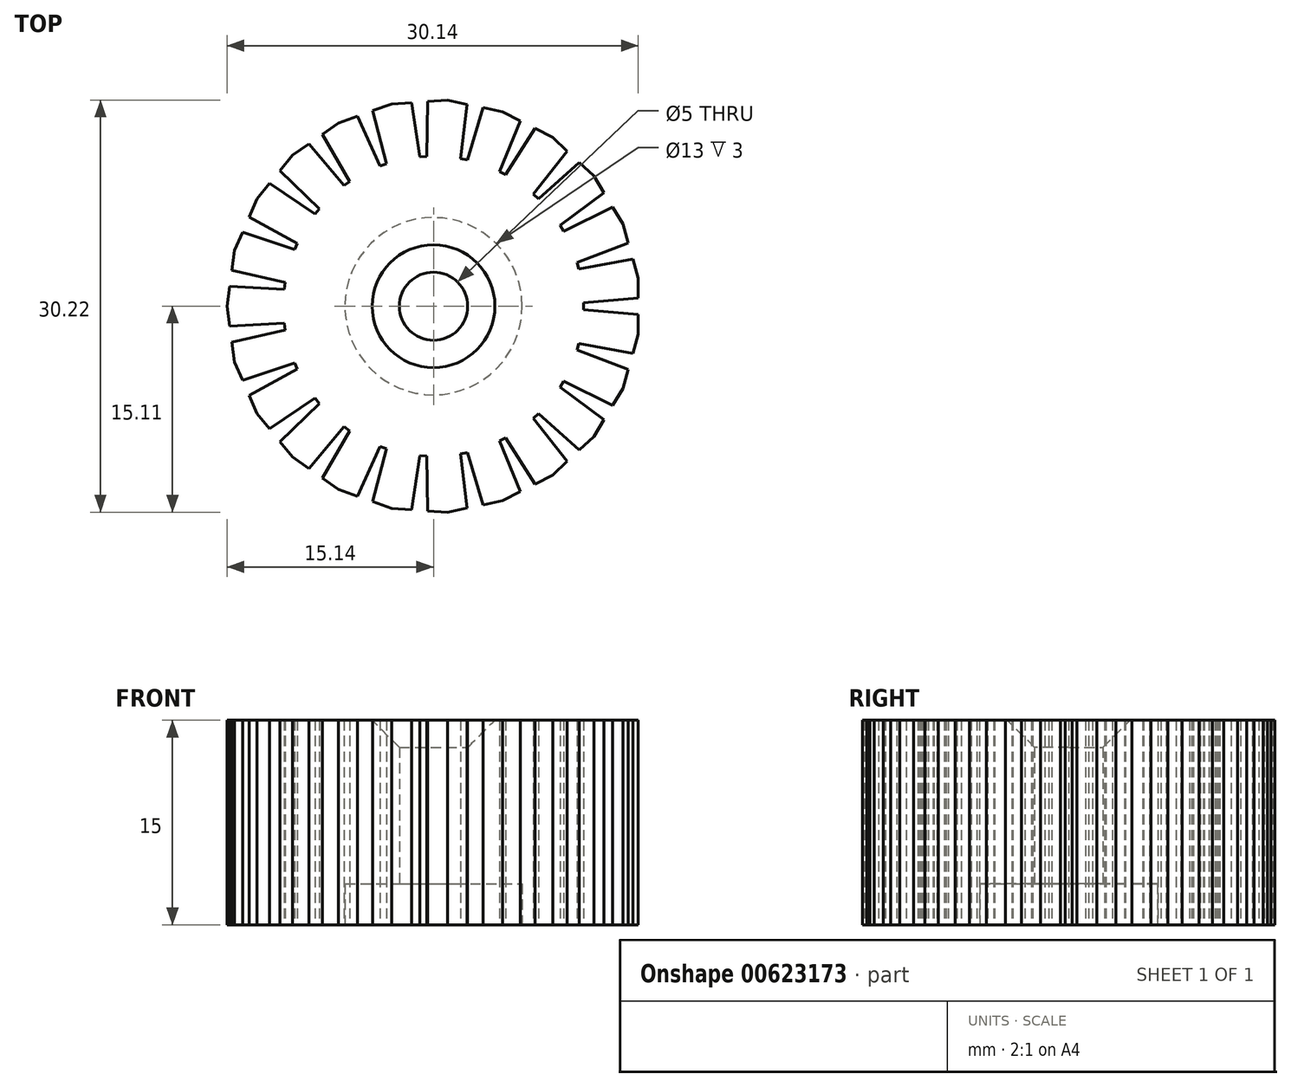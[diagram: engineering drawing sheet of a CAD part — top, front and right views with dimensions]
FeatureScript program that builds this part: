
annotation { "Feature Type Name" : "Feature", "Feature Type Description" : "" }
export const myFeature = defineFeature(function(context is Context, id is Id, definition is map)
    precondition{}
    {
        {
            var Q0;
            Q0=qCreatedBy(makeId("Top.planeOp"),FACE);
            var sketch = newSketch(context, id + "F0", { "sketchPlane" : qUnion([Q0])});
            skCircle(sketch, "E0", {"center": v(0, 0) * mm, "radius": 2.5 * mm});
            skCircle(sketch, "E1.cCircle", {"center": v(0, 0) * mm, "radius": 15 * mm, "construction": true});
            skLineSegment(sketch, "E1.0", {"start": v(15, 2.06) * mm, "end": v(15, 0.6) * mm});
            skLineSegment(sketch, "E1.1", {"start": v(15, -2.06) * mm, "end": v(13.89, -6.03) * mm, "construction": true});
            skLineSegment(sketch, "E1.2", {"start": v(13.89, -6.03) * mm, "end": v(11.75, -9.56) * mm, "construction": true});
            skLineSegment(sketch, "E1.3", {"start": v(11.75, -9.56) * mm, "end": v(8.73, -12.37) * mm, "construction": true});
            skLineSegment(sketch, "E1.4", {"start": v(8.73, -12.37) * mm, "end": v(5.07, -14.27) * mm, "construction": true});
            skLineSegment(sketch, "E1.5", {"start": v(5.07, -14.27) * mm, "end": v(1.03, -15.1) * mm, "construction": true});
            skLineSegment(sketch, "E1.6", {"start": v(1.03, -15.1) * mm, "end": v(-3.08, -14.82) * mm, "construction": true});
            skLineSegment(sketch, "E1.7", {"start": v(-3.08, -14.82) * mm, "end": v(-6.97, -13.44) * mm, "construction": true});
            skLineSegment(sketch, "E1.8", {"start": v(-6.97, -13.44) * mm, "end": v(-10.33, -11.07) * mm, "construction": true});
            skLineSegment(sketch, "E1.9", {"start": v(-10.33, -11.07) * mm, "end": v(-12.94, -7.87) * mm, "construction": true});
            skLineSegment(sketch, "E1.10", {"start": v(-12.94, -7.87) * mm, "end": v(-14.58, -4.08) * mm, "construction": true});
            skLineSegment(sketch, "E1.11", {"start": v(-14.58, -4.08) * mm, "end": v(-15.14, 0) * mm, "construction": true});
            skLineSegment(sketch, "E1.12", {"start": v(-15.14, 0) * mm, "end": v(-14.58, 4.08) * mm, "construction": true});
            skLineSegment(sketch, "E1.13", {"start": v(-14.58, 4.08) * mm, "end": v(-12.94, 7.87) * mm, "construction": true});
            skLineSegment(sketch, "E1.14", {"start": v(-12.94, 7.87) * mm, "end": v(-10.33, 11.07) * mm, "construction": true});
            skLineSegment(sketch, "E1.15", {"start": v(-10.33, 11.07) * mm, "end": v(-6.97, 13.44) * mm, "construction": true});
            skLineSegment(sketch, "E1.16", {"start": v(-6.97, 13.44) * mm, "end": v(-3.08, 14.82) * mm, "construction": true});
            skLineSegment(sketch, "E1.17", {"start": v(-3.08, 14.82) * mm, "end": v(1.03, 15.1) * mm, "construction": true});
            skLineSegment(sketch, "E1.18", {"start": v(1.03, 15.1) * mm, "end": v(5.07, 14.27) * mm, "construction": true});
            skLineSegment(sketch, "E1.19", {"start": v(5.07, 14.27) * mm, "end": v(8.73, 12.37) * mm, "construction": true});
            skLineSegment(sketch, "E1.20", {"start": v(8.73, 12.37) * mm, "end": v(11.75, 9.56) * mm, "construction": true});
            skLineSegment(sketch, "E1.21", {"start": v(11.75, 9.56) * mm, "end": v(13.89, 6.03) * mm, "construction": true});
            skLineSegment(sketch, "E1.22", {"start": v(13.89, 6.03) * mm, "end": v(15, 2.06) * mm, "construction": true});
            skPoint(sketch, "E1.0.midPoint", {"position": v(15, 0) * mm});
            skLineSegment(sketch, "E2", {"start": v(15, 0.6) * mm, "end": v(11, 0.25) * mm});
            skLineSegment(sketch, "E3", {"start": v(11, 0.25) * mm, "end": v(11, -0.25) * mm});
            skLineSegment(sketch, "E4", {"start": v(11, -0.25) * mm, "end": v(15, -0.6) * mm});
            skLineSegment(sketch, "E5.trimOffspring", {"start": v(15, -0.6) * mm, "end": v(15, -2.06) * mm});
            skLineSegment(sketch, "E6.1.0", {"start": v(13.89, 6.03) * mm, "end": v(14.28, 4.62) * mm});
            skLineSegment(sketch, "E6.1.1", {"start": v(14.28, 4.62) * mm, "end": v(10.52, 3.2) * mm});
            skLineSegment(sketch, "E6.1.2", {"start": v(10.66, 2.73) * mm, "end": v(14.6, 3.47) * mm});
            skLineSegment(sketch, "E6.1.3", {"start": v(10.52, 3.2) * mm, "end": v(10.66, 2.73) * mm});
            skLineSegment(sketch, "E6.1.4", {"start": v(14.6, 3.47) * mm, "end": v(15, 2.06) * mm});
            skLineSegment(sketch, "E6.2.0", {"start": v(11.75, 9.56) * mm, "end": v(12.5, 8.3) * mm});
            skLineSegment(sketch, "E6.2.1", {"start": v(12.5, 8.3) * mm, "end": v(9.27, 5.93) * mm});
            skLineSegment(sketch, "E6.2.2", {"start": v(9.53, 5.5) * mm, "end": v(13.13, 7.28) * mm});
            skLineSegment(sketch, "E6.2.3", {"start": v(9.27, 5.93) * mm, "end": v(9.53, 5.5) * mm});
            skLineSegment(sketch, "E6.2.4", {"start": v(13.13, 7.28) * mm, "end": v(13.89, 6.03) * mm});
            skLineSegment(sketch, "E6.3.0", {"start": v(8.73, 12.37) * mm, "end": v(9.8, 11.37) * mm});
            skLineSegment(sketch, "E6.3.1", {"start": v(9.8, 11.37) * mm, "end": v(7.33, 8.2) * mm});
            skLineSegment(sketch, "E6.3.2", {"start": v(7.7, 7.87) * mm, "end": v(10.68, 10.55) * mm});
            skLineSegment(sketch, "E6.3.3", {"start": v(7.33, 8.2) * mm, "end": v(7.7, 7.87) * mm});
            skLineSegment(sketch, "E6.3.4", {"start": v(10.68, 10.55) * mm, "end": v(11.75, 9.56) * mm});
            skLineSegment(sketch, "E6.4.0", {"start": v(5.07, 14.27) * mm, "end": v(6.37, 13.6) * mm});
            skLineSegment(sketch, "E6.4.1", {"start": v(6.37, 13.6) * mm, "end": v(4.84, 9.88) * mm});
            skLineSegment(sketch, "E6.4.2", {"start": v(5.28, 9.65) * mm, "end": v(7.43, 13.04) * mm});
            skLineSegment(sketch, "E6.4.3", {"start": v(4.84, 9.88) * mm, "end": v(5.28, 9.65) * mm});
            skLineSegment(sketch, "E6.4.4", {"start": v(7.43, 13.04) * mm, "end": v(8.73, 12.37) * mm});
            skLineSegment(sketch, "E6.5.0", {"start": v(1.03, 15.1) * mm, "end": v(2.46, 14.8) * mm});
            skLineSegment(sketch, "E6.5.1", {"start": v(2.46, 14.8) * mm, "end": v(2, 10.82) * mm});
            skLineSegment(sketch, "E6.5.2", {"start": v(2.48, 10.72) * mm, "end": v(3.64, 14.56) * mm});
            skLineSegment(sketch, "E6.5.3", {"start": v(2, 10.82) * mm, "end": v(2.48, 10.72) * mm});
            skLineSegment(sketch, "E6.5.4", {"start": v(3.64, 14.56) * mm, "end": v(5.07, 14.27) * mm});
            skLineSegment(sketch, "E6.6.0", {"start": v(-3.08, 14.82) * mm, "end": v(-1.62, 14.92) * mm});
            skLineSegment(sketch, "E6.6.1", {"start": v(-1.62, 14.92) * mm, "end": v(-1, 10.96) * mm});
            skLineSegment(sketch, "E6.6.2", {"start": v(-0.5, 11) * mm, "end": v(-0.43, 15) * mm});
            skLineSegment(sketch, "E6.6.3", {"start": v(-1, 10.96) * mm, "end": v(-0.5, 11) * mm});
            skLineSegment(sketch, "E6.6.4", {"start": v(-0.43, 15) * mm, "end": v(1.03, 15.1) * mm});
            skLineSegment(sketch, "E6.7.0", {"start": v(-6.97, 13.44) * mm, "end": v(-5.59, 13.93) * mm});
            skLineSegment(sketch, "E6.7.1", {"start": v(-5.59, 13.93) * mm, "end": v(-3.92, 10.28) * mm});
            skLineSegment(sketch, "E6.7.2", {"start": v(-3.45, 10.45) * mm, "end": v(-4.46, 14.33) * mm});
            skLineSegment(sketch, "E6.7.3", {"start": v(-3.92, 10.28) * mm, "end": v(-3.45, 10.45) * mm});
            skLineSegment(sketch, "E6.7.4", {"start": v(-4.46, 14.33) * mm, "end": v(-3.08, 14.82) * mm});
            skLineSegment(sketch, "E6.8.0", {"start": v(-10.33, 11.07) * mm, "end": v(-9.14, 11.9) * mm});
            skLineSegment(sketch, "E6.8.1", {"start": v(-9.14, 11.9) * mm, "end": v(-6.55, 8.84) * mm});
            skLineSegment(sketch, "E6.8.2", {"start": v(-6.14, 9.13) * mm, "end": v(-8.16, 12.6) * mm});
            skLineSegment(sketch, "E6.8.3", {"start": v(-6.55, 8.84) * mm, "end": v(-6.14, 9.13) * mm});
            skLineSegment(sketch, "E6.8.4", {"start": v(-8.16, 12.6) * mm, "end": v(-6.97, 13.44) * mm});
            skLineSegment(sketch, "E6.9.0", {"start": v(-12.94, 7.87) * mm, "end": v(-12.01, 9) * mm});
            skLineSegment(sketch, "E6.9.1", {"start": v(-12.01, 9) * mm, "end": v(-8.7, 6.75) * mm});
            skLineSegment(sketch, "E6.9.2", {"start": v(-8.38, 7.14) * mm, "end": v(-11.26, 9.93) * mm});
            skLineSegment(sketch, "E6.9.3", {"start": v(-8.7, 6.75) * mm, "end": v(-8.38, 7.14) * mm});
            skLineSegment(sketch, "E6.9.4", {"start": v(-11.26, 9.93) * mm, "end": v(-10.33, 11.07) * mm});
            skLineSegment(sketch, "E6.10.0", {"start": v(-14.58, 4.08) * mm, "end": v(-14, 5.43) * mm});
            skLineSegment(sketch, "E6.10.1", {"start": v(-14, 5.43) * mm, "end": v(-10.19, 4.15) * mm});
            skLineSegment(sketch, "E6.10.2", {"start": v(-9.99, 4.61) * mm, "end": v(-13.52, 6.53) * mm});
            skLineSegment(sketch, "E6.10.3", {"start": v(-10.19, 4.15) * mm, "end": v(-9.99, 4.61) * mm});
            skLineSegment(sketch, "E6.10.4", {"start": v(-13.52, 6.53) * mm, "end": v(-12.94, 7.87) * mm});
            skLineSegment(sketch, "E6.11.0", {"start": v(-15.14, 0) * mm, "end": v(-14.94, 1.45) * mm});
            skLineSegment(sketch, "E6.11.1", {"start": v(-14.94, 1.45) * mm, "end": v(-10.93, 1.25) * mm});
            skLineSegment(sketch, "E6.11.2", {"start": v(-10.86, 1.75) * mm, "end": v(-14.78, 2.64) * mm});
            skLineSegment(sketch, "E6.11.3", {"start": v(-10.93, 1.25) * mm, "end": v(-10.86, 1.75) * mm});
            skLineSegment(sketch, "E6.11.4", {"start": v(-14.78, 2.64) * mm, "end": v(-14.58, 4.08) * mm});
            skLineSegment(sketch, "E6.12.0", {"start": v(-14.58, -4.08) * mm, "end": v(-14.78, -2.64) * mm});
            skLineSegment(sketch, "E6.12.1", {"start": v(-14.78, -2.64) * mm, "end": v(-10.86, -1.75) * mm});
            skLineSegment(sketch, "E6.12.2", {"start": v(-10.93, -1.25) * mm, "end": v(-14.94, -1.45) * mm});
            skLineSegment(sketch, "E6.12.3", {"start": v(-10.86, -1.75) * mm, "end": v(-10.93, -1.25) * mm});
            skLineSegment(sketch, "E6.12.4", {"start": v(-14.94, -1.45) * mm, "end": v(-15.14, 0) * mm});
            skLineSegment(sketch, "E6.13.0", {"start": v(-12.94, -7.87) * mm, "end": v(-13.52, -6.53) * mm});
            skLineSegment(sketch, "E6.13.1", {"start": v(-13.52, -6.53) * mm, "end": v(-9.99, -4.61) * mm});
            skLineSegment(sketch, "E6.13.2", {"start": v(-10.19, -4.15) * mm, "end": v(-14, -5.43) * mm});
            skLineSegment(sketch, "E6.13.3", {"start": v(-9.99, -4.61) * mm, "end": v(-10.19, -4.15) * mm});
            skLineSegment(sketch, "E6.13.4", {"start": v(-14, -5.43) * mm, "end": v(-14.58, -4.08) * mm});
            skLineSegment(sketch, "E6.14.0", {"start": v(-10.33, -11.07) * mm, "end": v(-11.26, -9.93) * mm});
            skLineSegment(sketch, "E6.14.1", {"start": v(-11.26, -9.93) * mm, "end": v(-8.38, -7.14) * mm});
            skLineSegment(sketch, "E6.14.2", {"start": v(-8.7, -6.75) * mm, "end": v(-12.01, -9) * mm});
            skLineSegment(sketch, "E6.14.3", {"start": v(-8.38, -7.14) * mm, "end": v(-8.7, -6.75) * mm});
            skLineSegment(sketch, "E6.14.4", {"start": v(-12.01, -9) * mm, "end": v(-12.94, -7.87) * mm});
            skLineSegment(sketch, "E6.15.0", {"start": v(-6.97, -13.44) * mm, "end": v(-8.16, -12.6) * mm});
            skLineSegment(sketch, "E6.15.1", {"start": v(-8.16, -12.6) * mm, "end": v(-6.14, -9.13) * mm});
            skLineSegment(sketch, "E6.15.2", {"start": v(-6.55, -8.84) * mm, "end": v(-9.14, -11.9) * mm});
            skLineSegment(sketch, "E6.15.3", {"start": v(-6.14, -9.13) * mm, "end": v(-6.55, -8.84) * mm});
            skLineSegment(sketch, "E6.15.4", {"start": v(-9.14, -11.9) * mm, "end": v(-10.33, -11.07) * mm});
            skLineSegment(sketch, "E6.16.0", {"start": v(-3.08, -14.82) * mm, "end": v(-4.46, -14.33) * mm});
            skLineSegment(sketch, "E6.16.1", {"start": v(-4.46, -14.33) * mm, "end": v(-3.45, -10.45) * mm});
            skLineSegment(sketch, "E6.16.2", {"start": v(-3.92, -10.28) * mm, "end": v(-5.59, -13.93) * mm});
            skLineSegment(sketch, "E6.16.3", {"start": v(-3.45, -10.45) * mm, "end": v(-3.92, -10.28) * mm});
            skLineSegment(sketch, "E6.16.4", {"start": v(-5.59, -13.93) * mm, "end": v(-6.97, -13.44) * mm});
            skLineSegment(sketch, "E6.17.0", {"start": v(1.03, -15.1) * mm, "end": v(-0.43, -15) * mm});
            skLineSegment(sketch, "E6.17.1", {"start": v(-0.43, -15) * mm, "end": v(-0.5, -11) * mm});
            skLineSegment(sketch, "E6.17.2", {"start": v(-1, -10.96) * mm, "end": v(-1.62, -14.92) * mm});
            skLineSegment(sketch, "E6.17.3", {"start": v(-0.5, -11) * mm, "end": v(-1, -10.96) * mm});
            skLineSegment(sketch, "E6.17.4", {"start": v(-1.62, -14.92) * mm, "end": v(-3.08, -14.82) * mm});
            skLineSegment(sketch, "E6.18.0", {"start": v(5.07, -14.27) * mm, "end": v(3.64, -14.56) * mm});
            skLineSegment(sketch, "E6.18.1", {"start": v(3.64, -14.56) * mm, "end": v(2.48, -10.72) * mm});
            skLineSegment(sketch, "E6.18.2", {"start": v(2, -10.82) * mm, "end": v(2.46, -14.8) * mm});
            skLineSegment(sketch, "E6.18.3", {"start": v(2.48, -10.72) * mm, "end": v(2, -10.82) * mm});
            skLineSegment(sketch, "E6.18.4", {"start": v(2.46, -14.8) * mm, "end": v(1.03, -15.1) * mm});
            skLineSegment(sketch, "E6.19.0", {"start": v(8.73, -12.37) * mm, "end": v(7.43, -13.04) * mm});
            skLineSegment(sketch, "E6.19.1", {"start": v(7.43, -13.04) * mm, "end": v(5.28, -9.65) * mm});
            skLineSegment(sketch, "E6.19.2", {"start": v(4.84, -9.88) * mm, "end": v(6.37, -13.6) * mm});
            skLineSegment(sketch, "E6.19.3", {"start": v(5.28, -9.65) * mm, "end": v(4.84, -9.88) * mm});
            skLineSegment(sketch, "E6.19.4", {"start": v(6.37, -13.6) * mm, "end": v(5.07, -14.27) * mm});
            skLineSegment(sketch, "E6.20.0", {"start": v(11.75, -9.56) * mm, "end": v(10.68, -10.55) * mm});
            skLineSegment(sketch, "E6.20.1", {"start": v(10.68, -10.55) * mm, "end": v(7.7, -7.87) * mm});
            skLineSegment(sketch, "E6.20.2", {"start": v(7.33, -8.2) * mm, "end": v(9.8, -11.37) * mm});
            skLineSegment(sketch, "E6.20.3", {"start": v(7.7, -7.87) * mm, "end": v(7.33, -8.2) * mm});
            skLineSegment(sketch, "E6.20.4", {"start": v(9.8, -11.37) * mm, "end": v(8.73, -12.37) * mm});
            skLineSegment(sketch, "E6.21.0", {"start": v(13.89, -6.03) * mm, "end": v(13.13, -7.28) * mm});
            skLineSegment(sketch, "E6.21.1", {"start": v(13.13, -7.28) * mm, "end": v(9.53, -5.5) * mm});
            skLineSegment(sketch, "E6.21.2", {"start": v(9.27, -5.93) * mm, "end": v(12.5, -8.3) * mm});
            skLineSegment(sketch, "E6.21.3", {"start": v(9.53, -5.5) * mm, "end": v(9.27, -5.93) * mm});
            skLineSegment(sketch, "E6.21.4", {"start": v(12.5, -8.3) * mm, "end": v(11.75, -9.56) * mm});
            skLineSegment(sketch, "E6.22.0", {"start": v(15, -2.06) * mm, "end": v(14.6, -3.47) * mm});
            skLineSegment(sketch, "E6.22.1", {"start": v(14.6, -3.47) * mm, "end": v(10.66, -2.73) * mm});
            skLineSegment(sketch, "E6.22.2", {"start": v(10.52, -3.2) * mm, "end": v(14.28, -4.62) * mm});
            skLineSegment(sketch, "E6.22.3", {"start": v(10.66, -2.73) * mm, "end": v(10.52, -3.2) * mm});
            skLineSegment(sketch, "E6.22.4", {"start": v(14.28, -4.62) * mm, "end": v(13.89, -6.03) * mm});
            skSolve(sketch);
        }
        {
            var Q0;
            Q0 = qSketchRegion(id + "F0", true);
            extrude(context, id + "F1", {"entities" : qUnion([Q0]), "depth" : 15 * mm, "offsetDistance" : 25 * mm});
        }
        {
            var Q0;
            Q0=makeQuery(id+"F1.opExtrude","CAP_FACE",FACE,{"disambiguationData":[OSD([sQuery(id+"F0.wireOp",EDGE,"E0"),sQuery(id+"F0.wireOp",EDGE,"E1.0"),sQuery(id+"F0.wireOp",EDGE,"E2"),sQuery(id+"F0.wireOp",EDGE,"E3"),sQuery(id+"F0.wireOp",EDGE,"E4"),sQuery(id+"F0.wireOp",EDGE,"E5.trimOffspring"),sQuery(id+"F0.wireOp",EDGE,"E6.1.0"),sQuery(id+"F0.wireOp",EDGE,"E6.1.1"),sQuery(id+"F0.wireOp",EDGE,"E6.1.2"),sQuery(id+"F0.wireOp",EDGE,"E6.1.3"),sQuery(id+"F0.wireOp",EDGE,"E6.1.4"),sQuery(id+"F0.wireOp",EDGE,"E6.2.0"),sQuery(id+"F0.wireOp",EDGE,"E6.2.1"),sQuery(id+"F0.wireOp",EDGE,"E6.2.2"),sQuery(id+"F0.wireOp",EDGE,"E6.2.3"),sQuery(id+"F0.wireOp",EDGE,"E6.2.4"),sQuery(id+"F0.wireOp",EDGE,"E6.3.0"),sQuery(id+"F0.wireOp",EDGE,"E6.3.1"),sQuery(id+"F0.wireOp",EDGE,"E6.3.2"),sQuery(id+"F0.wireOp",EDGE,"E6.3.3"),sQuery(id+"F0.wireOp",EDGE,"E6.3.4"),sQuery(id+"F0.wireOp",EDGE,"E6.4.0"),sQuery(id+"F0.wireOp",EDGE,"E6.4.1"),sQuery(id+"F0.wireOp",EDGE,"E6.4.2"),sQuery(id+"F0.wireOp",EDGE,"E6.4.3"),sQuery(id+"F0.wireOp",EDGE,"E6.4.4"),sQuery(id+"F0.wireOp",EDGE,"E6.5.0"),sQuery(id+"F0.wireOp",EDGE,"E6.5.1"),sQuery(id+"F0.wireOp",EDGE,"E6.5.2"),sQuery(id+"F0.wireOp",EDGE,"E6.5.3"),sQuery(id+"F0.wireOp",EDGE,"E6.5.4"),sQuery(id+"F0.wireOp",EDGE,"E6.6.0"),sQuery(id+"F0.wireOp",EDGE,"E6.6.1"),sQuery(id+"F0.wireOp",EDGE,"E6.6.2"),sQuery(id+"F0.wireOp",EDGE,"E6.6.3"),sQuery(id+"F0.wireOp",EDGE,"E6.6.4"),sQuery(id+"F0.wireOp",EDGE,"E6.7.0"),sQuery(id+"F0.wireOp",EDGE,"E6.7.1"),sQuery(id+"F0.wireOp",EDGE,"E6.7.2"),sQuery(id+"F0.wireOp",EDGE,"E6.7.3"),sQuery(id+"F0.wireOp",EDGE,"E6.7.4"),sQuery(id+"F0.wireOp",EDGE,"E6.8.0"),sQuery(id+"F0.wireOp",EDGE,"E6.8.1"),sQuery(id+"F0.wireOp",EDGE,"E6.8.2"),sQuery(id+"F0.wireOp",EDGE,"E6.8.3"),sQuery(id+"F0.wireOp",EDGE,"E6.8.4"),sQuery(id+"F0.wireOp",EDGE,"E6.9.0"),sQuery(id+"F0.wireOp",EDGE,"E6.9.1"),sQuery(id+"F0.wireOp",EDGE,"E6.9.2"),sQuery(id+"F0.wireOp",EDGE,"E6.9.3"),sQuery(id+"F0.wireOp",EDGE,"E6.9.4"),sQuery(id+"F0.wireOp",EDGE,"E6.10.0"),sQuery(id+"F0.wireOp",EDGE,"E6.10.1"),sQuery(id+"F0.wireOp",EDGE,"E6.10.2"),sQuery(id+"F0.wireOp",EDGE,"E6.10.3"),sQuery(id+"F0.wireOp",EDGE,"E6.10.4"),sQuery(id+"F0.wireOp",EDGE,"E6.11.0"),sQuery(id+"F0.wireOp",EDGE,"E6.11.1"),sQuery(id+"F0.wireOp",EDGE,"E6.11.2"),sQuery(id+"F0.wireOp",EDGE,"E6.11.3"),sQuery(id+"F0.wireOp",EDGE,"E6.11.4"),sQuery(id+"F0.wireOp",EDGE,"E6.12.0"),sQuery(id+"F0.wireOp",EDGE,"E6.12.1"),sQuery(id+"F0.wireOp",EDGE,"E6.12.2"),sQuery(id+"F0.wireOp",EDGE,"E6.12.3"),sQuery(id+"F0.wireOp",EDGE,"E6.12.4"),sQuery(id+"F0.wireOp",EDGE,"E6.13.0"),sQuery(id+"F0.wireOp",EDGE,"E6.13.1"),sQuery(id+"F0.wireOp",EDGE,"E6.13.2"),sQuery(id+"F0.wireOp",EDGE,"E6.13.3"),sQuery(id+"F0.wireOp",EDGE,"E6.13.4"),sQuery(id+"F0.wireOp",EDGE,"E6.14.0"),sQuery(id+"F0.wireOp",EDGE,"E6.14.1"),sQuery(id+"F0.wireOp",EDGE,"E6.14.2"),sQuery(id+"F0.wireOp",EDGE,"E6.14.3"),sQuery(id+"F0.wireOp",EDGE,"E6.14.4"),sQuery(id+"F0.wireOp",EDGE,"E6.15.0"),sQuery(id+"F0.wireOp",EDGE,"E6.15.1"),sQuery(id+"F0.wireOp",EDGE,"E6.15.2"),sQuery(id+"F0.wireOp",EDGE,"E6.15.3"),sQuery(id+"F0.wireOp",EDGE,"E6.15.4"),sQuery(id+"F0.wireOp",EDGE,"E6.16.0"),sQuery(id+"F0.wireOp",EDGE,"E6.16.1"),sQuery(id+"F0.wireOp",EDGE,"E6.16.2"),sQuery(id+"F0.wireOp",EDGE,"E6.16.3"),sQuery(id+"F0.wireOp",EDGE,"E6.16.4"),sQuery(id+"F0.wireOp",EDGE,"E6.17.0"),sQuery(id+"F0.wireOp",EDGE,"E6.17.1"),sQuery(id+"F0.wireOp",EDGE,"E6.17.2"),sQuery(id+"F0.wireOp",EDGE,"E6.17.3"),sQuery(id+"F0.wireOp",EDGE,"E6.17.4"),sQuery(id+"F0.wireOp",EDGE,"E6.18.0"),sQuery(id+"F0.wireOp",EDGE,"E6.18.1"),sQuery(id+"F0.wireOp",EDGE,"E6.18.2"),sQuery(id+"F0.wireOp",EDGE,"E6.18.3"),sQuery(id+"F0.wireOp",EDGE,"E6.18.4"),sQuery(id+"F0.wireOp",EDGE,"E6.19.0"),sQuery(id+"F0.wireOp",EDGE,"E6.19.1"),sQuery(id+"F0.wireOp",EDGE,"E6.19.2"),sQuery(id+"F0.wireOp",EDGE,"E6.19.3"),sQuery(id+"F0.wireOp",EDGE,"E6.19.4"),sQuery(id+"F0.wireOp",EDGE,"E6.20.0"),sQuery(id+"F0.wireOp",EDGE,"E6.20.1"),sQuery(id+"F0.wireOp",EDGE,"E6.20.2"),sQuery(id+"F0.wireOp",EDGE,"E6.20.3"),sQuery(id+"F0.wireOp",EDGE,"E6.20.4"),sQuery(id+"F0.wireOp",EDGE,"E6.21.0"),sQuery(id+"F0.wireOp",EDGE,"E6.21.1"),sQuery(id+"F0.wireOp",EDGE,"E6.21.2"),sQuery(id+"F0.wireOp",EDGE,"E6.21.3"),sQuery(id+"F0.wireOp",EDGE,"E6.21.4"),sQuery(id+"F0.wireOp",EDGE,"E6.22.0"),sQuery(id+"F0.wireOp",EDGE,"E6.22.1"),sQuery(id+"F0.wireOp",EDGE,"E6.22.2"),sQuery(id+"F0.wireOp",EDGE,"E6.22.3"),sQuery(id+"F0.wireOp",EDGE,"E6.22.4")])],"isStart":true});
            var sketch = newSketch(context, id + "F2", { "sketchPlane" : qUnion([Q0])});
            skCircle(sketch, "E7", {"center": v(0, 0) * mm, "radius": 6.5 * mm});
            skSolve(sketch);
        }
        {
            var Q0;
            Q0 = qSketchRegion(id + "F2", true);
            extrude(context, id + "F3", {"entities" : qUnion([Q0]), "operationType" : NewBodyOperationType.REMOVE, "oppositeDirection" : true, "depth" : 3 * mm, "offsetDistance" : 25 * mm});
        }
        {
            var Q0;
            Q0=makeQuery(id+"F1.opExtrude","CAP_EDGE",EDGE,{"disambiguationData":[OSD([sQuery(id+"F0.wireOp",EDGE,"E0")])],"isStart":false});
            chamfer(context, id + "F4", {"entities" : qUnion([Q0]), "width" : 2 * mm, "tangentPropagation" : true});
        }
    });
